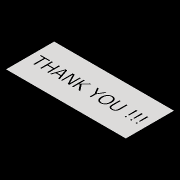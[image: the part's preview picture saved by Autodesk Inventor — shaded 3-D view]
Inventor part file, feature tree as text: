
AUTODESK INVENTOR PART (.ipt)
format: ipt  version: 2018 (Build 220112000, 112)  size: 150,016 bytes
history: native  units: mm
features: plane x1, sketch x1, other x1, surface_op x1
ambient origin geometry x8: Origin, YZ Plane, XZ Plane, XY Plane, X Axis, Y Axis, Z Axis, Center Point
bodies: Body1 (feature_tree)
feature tree (4):
  plane  "Work Plane1"
  sketch  "Sketch2"  dims[d6=10.0mm d7=25.0mm d8=10.0mm]
  other  "Srf1"
  surface_op  "Boundary Patch1"
